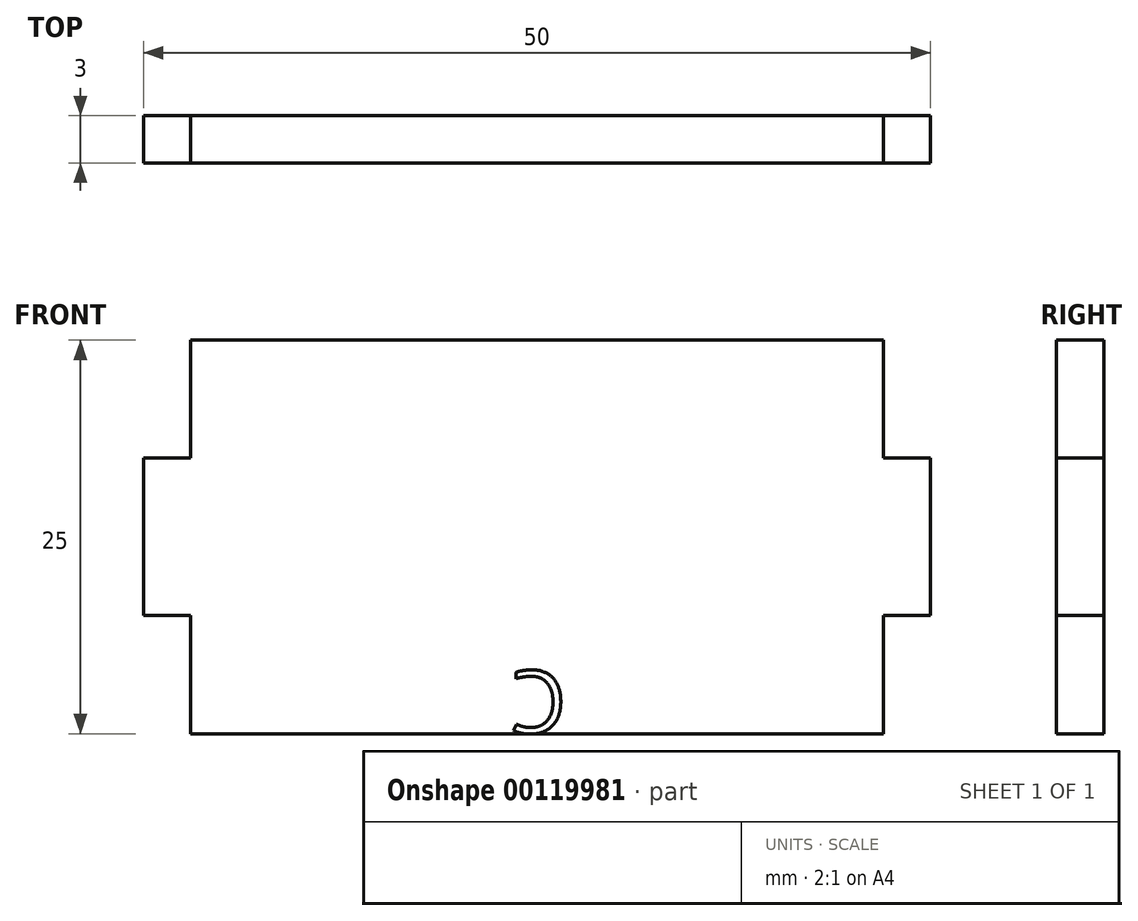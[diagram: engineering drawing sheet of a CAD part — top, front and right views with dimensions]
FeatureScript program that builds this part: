
annotation { "Feature Type Name" : "Feature", "Feature Type Description" : "" }
export const myFeature = defineFeature(function(context is Context, id is Id, definition is map)
    precondition{}
    {
        {
            var Q0;
            Q0=qCreatedBy(makeId("Front.planeOp"),FACE);
            var sketch = newSketch(context, id + "F0", { "sketchPlane" : qUnion([Q0])});
            skLineSegment(sketch, "E0.bottom", {"start": v(0, 0) * mm, "end": v(-44, 0) * mm});
            skLineSegment(sketch, "E0.top", {"start": v(0, 25) * mm, "end": v(-44, 25) * mm});
            skLineSegment(sketch, "E0.left", {"start": v(0, 0) * mm, "end": v(0, 25) * mm});
            skLineSegment(sketch, "E0.right", {"start": v(-44, 0) * mm, "end": v(-44, 25) * mm});
            skLineSegment(sketch, "E1.bottom", {"start": v(-44, 17.5) * mm, "end": v(-47, 17.5) * mm});
            skLineSegment(sketch, "E1.top", {"start": v(-44, 7.5) * mm, "end": v(-47, 7.5) * mm});
            skLineSegment(sketch, "E1.left", {"start": v(-44, 17.5) * mm, "end": v(-44, 7.5) * mm});
            skLineSegment(sketch, "E1.right", {"start": v(-47, 17.5) * mm, "end": v(-47, 7.5) * mm});
            skLineSegment(sketch, "E2", {"start": v(-44, 12.5) * mm, "end": v(-47, 12.5) * mm, "construction": true});
            skLineSegment(sketch, "E3", {"start": v(-22, 25) * mm, "end": v(-22, 0) * mm, "construction": true});
            skLineSegment(sketch, "E4.MirrorCS", {"start": v(0, 17.5) * mm, "end": v(3, 17.5) * mm});
            skLineSegment(sketch, "E5.MirrorCS", {"start": v(3, 17.5) * mm, "end": v(3, 7.5) * mm});
            skLineSegment(sketch, "E6.MirrorCS", {"start": v(0, 12.5) * mm, "end": v(3, 12.5) * mm, "construction": true});
            skLineSegment(sketch, "E7.MirrorCS", {"start": v(0, 7.5) * mm, "end": v(3, 7.5) * mm});
            skLineSegment(sketch, "E8.bottom", {"start": v(-27, 0) * mm, "end": v(-17, 0) * mm});
            skLineSegment(sketch, "E8.top", {"start": v(-27, -3) * mm, "end": v(-17, -3) * mm});
            skLineSegment(sketch, "E8.left", {"start": v(-27, 0) * mm, "end": v(-27, -3) * mm});
            skLineSegment(sketch, "E8.right", {"start": v(-17, 0) * mm, "end": v(-17, -3) * mm});
            skSolve(sketch);
        }
        {
            var Q0;
            {var subQ5=sQuery(id+"F0.wireOp",EDGE,"E0.top");Q0=makeQuery(id+"F0.imprint","IMPRINT",FACE,{"disambiguationData":[TD([[makeQuery(id+"F0.imprint","IMPRINT",EDGE,{"derivedFrom":subQ5}),1.0]])]});}
            var Q1;
            {var subQ0=sQuery(id+"F0.wireOp",EDGE,"E4.MirrorCS");Q1=makeQuery(id+"F0.imprint","IMPRINT",FACE,{"disambiguationData":[TD([[makeQuery(id+"F0.imprint","IMPRINT",EDGE,{"derivedFrom":subQ0}),-1.0]])]});}
            var Q2;
            Q2=makeQuery(id+"F0.imprint","IMPRINT",FACE,{"disambiguationData":[TD([[makeQuery(id+"F0.imprint","IMPRINT",EDGE,{"derivedFrom":sQuery(id+"F0.wireOp",EDGE,"E1.bottom")}),1.0]])]});
            var Q3;
            Q3=makeQuery(id+"F0.imprint","IMPRINT",FACE,{"disambiguationData":[TD([[makeQuery(id+"F0.imprint","IMPRINT",EDGE,{"derivedFrom":sQuery(id+"F0.wireOp",EDGE,"E8.bottom")}),-1.0]])]});
            extrude(context, id + "F1", {"entities" : qUnion([Q0, Q1, Q2, Q3]), "depth" : 3 * mm});
        }
        {
            var Q0;
            Q0=makeQuery(id+"F1.opExtrude","CAP_FACE",FACE,{"disambiguationData":[OSD([sQuery(id+"F0.wireOp",EDGE,"E0.bottom"),sQuery(id+"F0.wireOp",EDGE,"E0.top"),sQuery(id+"F0.wireOp",EDGE,"E0.left"),sQuery(id+"F0.wireOp",EDGE,"E0.right"),sQuery(id+"F0.wireOp",EDGE,"E1.bottom"),sQuery(id+"F0.wireOp",EDGE,"E1.top"),sQuery(id+"F0.wireOp",EDGE,"E1.right"),sQuery(id+"F0.wireOp",EDGE,"E4.MirrorCS"),sQuery(id+"F0.wireOp",EDGE,"E5.MirrorCS"),sQuery(id+"F0.wireOp",EDGE,"E7.MirrorCS"),sQuery(id+"F0.wireOp",EDGE,"E8.top"),sQuery(id+"F0.wireOp",EDGE,"E8.left"),sQuery(id+"F0.wireOp",EDGE,"E8.right")])],"isStart":false});
            var sketch = newSketch(context, id + "F2", { "sketchPlane" : qUnion([Q0])});
            skText(sketch, "E9", { "text": "C", "fontName": "OpenSans-Regular.ttf"});
            const initialGuessF2  = {"E9": [-0.02015, 0.004, -1, 0, 0.004]};
            skSetInitialGuess(sketch, initialGuessF2);
            skSolve(sketch);
        }
        {
            var Q0;
            Q0=makeQuery(id+"F2.imprint","IMPRINT",FACE,{"disambiguationData":[TD([[makeQuery(id+"F2.imprint","IMPRINT",EDGE,{"derivedFrom":sQuery(id+"F2.wireOp",EDGE,"E9.sketch_text.stroke-0")}),-1.0]])]});
            extrude(context, id + "F3", {"entities" : qUnion([Q0]), "operationType" : NewBodyOperationType.ADD, "depth" : 0 * mm});
        }
    });
